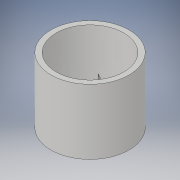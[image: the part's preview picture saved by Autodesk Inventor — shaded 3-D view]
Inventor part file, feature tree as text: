
AUTODESK INVENTOR PART (.ipt)
format: ipt  version: 2019 (Build 230136000, 136)  size: 115,712 bytes
history: native  units: mm
features: extrude x2, sketch x2
ambient origin geometry x8: Origin, YZ Plane, XZ Plane, XY Plane, X Axis, Y Axis, Z Axis, Center Point
bodies: Solid1 (feature_tree)
feature tree (4):
  extrude  "Extrusion1"  Depth=52.0mm
  extrude  "Extrusion2"  Depth=30.0mm TaperAngle=0.0deg
  sketch  "Sketch1"  dims[d0=60.0mm d1=52.0mm]
  sketch  "Sketch2"  dims[d2=50.0mm d3=0.0mm d4=30.0mm d5=0.0mm d6=15.0deg d7=15.0deg]
